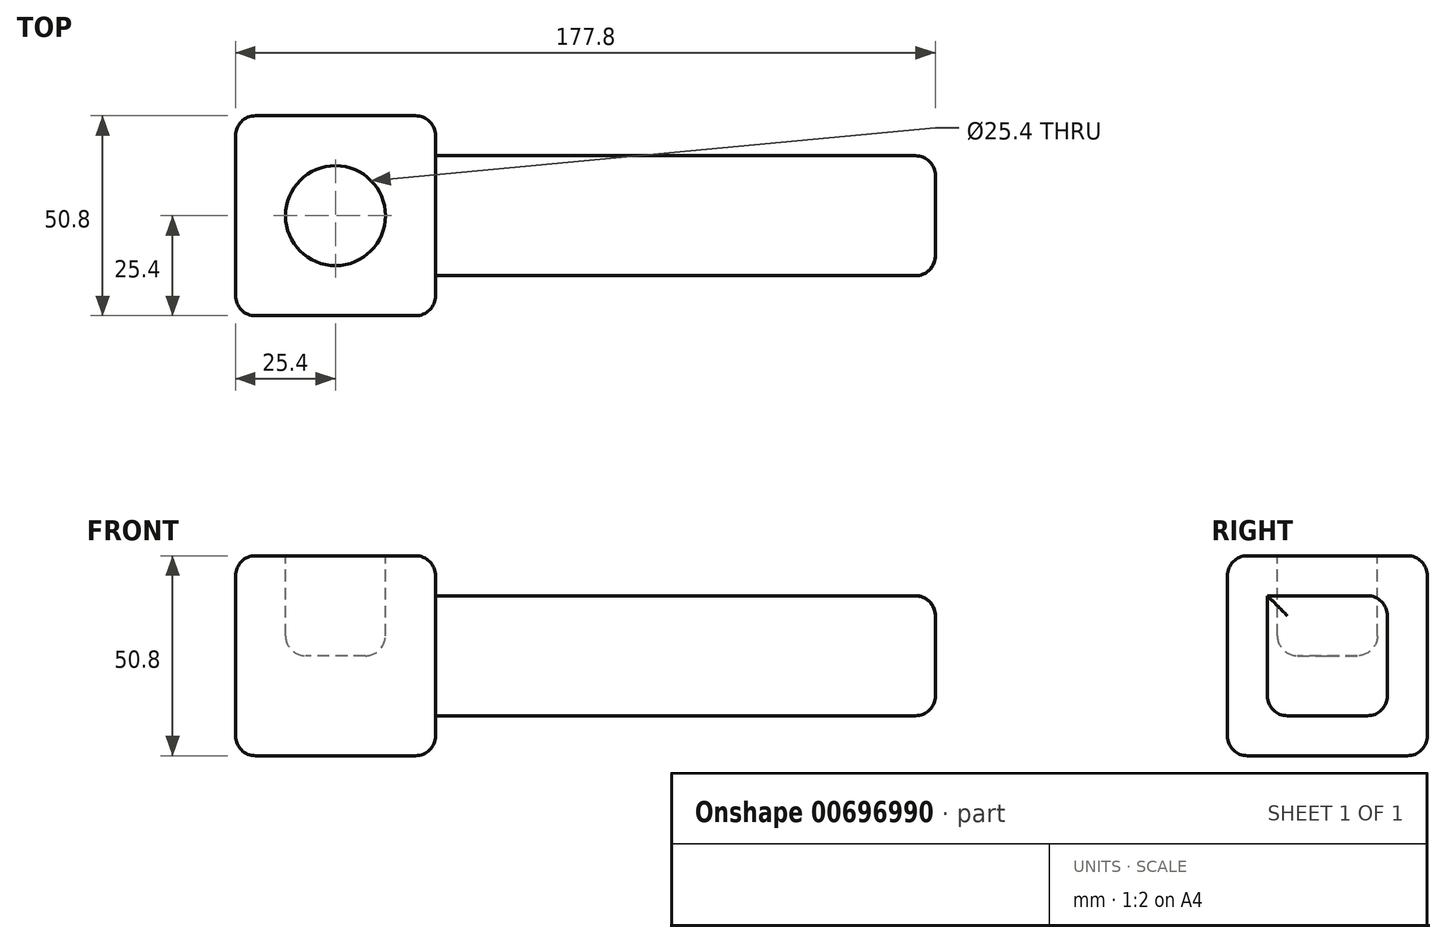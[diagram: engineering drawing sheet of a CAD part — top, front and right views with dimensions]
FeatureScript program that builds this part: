
annotation { "Feature Type Name" : "Feature", "Feature Type Description" : "" }
export const myFeature = defineFeature(function(context is Context, id is Id, definition is map)
    precondition{}
    {
        {
            var Q0;
            Q0=qCreatedBy(makeId("Top.planeOp"),FACE);
            var sketch = newSketch(context, id + "F0", { "sketchPlane" : qUnion([Q0])});
            skLineSegment(sketch, "E0.bottom", {"start": v(0, 0) * mm, "end": v(50.8, 0) * mm});
            skLineSegment(sketch, "E0.top", {"start": v(0, 50.8) * mm, "end": v(50.8, 50.8) * mm});
            skLineSegment(sketch, "E0.left", {"start": v(0, 0) * mm, "end": v(0, 50.8) * mm});
            skLineSegment(sketch, "E0.right", {"start": v(50.8, 0) * mm, "end": v(50.8, 50.8) * mm});
            skSolve(sketch);
        }
        {
            var Q0;
            Q0 = qSketchRegion(id + "F0", true);
            extrude(context, id + "F1", {"entities" : qUnion([Q0]), "depth" : 50.8 * mm, "offsetDistance" : 25.4 * mm});
        }
        {
            var Q0;
            Q0=makeQuery(id+"F1.opExtrude","CAP_FACE",FACE,{"disambiguationData":[OSD([sQuery(id+"F0.wireOp",EDGE,"E0.bottom"),sQuery(id+"F0.wireOp",EDGE,"E0.top"),sQuery(id+"F0.wireOp",EDGE,"E0.left"),sQuery(id+"F0.wireOp",EDGE,"E0.right")])],"isStart":false});
            var sketch = newSketch(context, id + "F2", { "sketchPlane" : qUnion([Q0])});
            skLineSegment(sketch, "E1", {"start": v(0, 0) * mm, "end": v(50.8, 50.8) * mm, "construction": true});
            skLineSegment(sketch, "E2", {"start": v(50.8, 0) * mm, "end": v(0, 50.8) * mm, "construction": true});
            skLineSegment(sketch, "E3", {"start": v(0, 50.8) * mm, "end": v(0.46, 49.47) * mm});
            skCircle(sketch, "E4", {"center": v(25.4, 25.4) * mm, "radius": 12.7 * mm});
            skSolve(sketch);
        }
        {
            var Q0;
            Q0 = qSketchRegion(id + "F2", true);
            extrude(context, id + "F3", {"entities" : qUnion([Q0]), "operationType" : NewBodyOperationType.REMOVE, "oppositeDirection" : true, "depth" : 25.4 * mm, "offsetDistance" : 25.4 * mm});
        }
        {
            var Q0;
            Q0=makeQuery(id+"F1.opExtrude","CAP_EDGE",EDGE,{"disambiguationData":[OSD([sQuery(id+"F0.wireOp",EDGE,"E0.top")])],"isStart":false});
            var Q1;
            Q1=makeQuery(id+"F1.opExtrude","CAP_EDGE",EDGE,{"disambiguationData":[OSD([sQuery(id+"F0.wireOp",EDGE,"E0.right")])],"isStart":false});
            var Q2;
            Q2=makeQuery(id+"F1.opExtrude","CAP_EDGE",EDGE,{"disambiguationData":[OSD([sQuery(id+"F0.wireOp",EDGE,"E0.bottom")])],"isStart":false});
            var Q3;
            Q3=makeQuery(id+"F1.opExtrude","CAP_EDGE",EDGE,{"disambiguationData":[OSD([sQuery(id+"F0.wireOp",EDGE,"E0.left")])],"isStart":false});
            var Q4;
            Q4=makeQuery(id+"F1.opExtrude","SWEPT_FACE",FACE,{"disambiguationData":[OSD([sQuery(id+"F0.wireOp",EDGE,"E0.right")])]});
            var Q5;
            Q5=makeQuery(id+"F1.opExtrude","SWEPT_FACE",FACE,{"disambiguationData":[OSD([sQuery(id+"F0.wireOp",EDGE,"E0.bottom")])]});
            var Q6;
            Q6=makeQuery(id+"F1.opExtrude","SWEPT_FACE",FACE,{"disambiguationData":[OSD([sQuery(id+"F0.wireOp",EDGE,"E0.left")])]});
            var Q7;
            Q7=makeQuery(id+"F1.opExtrude","CAP_FACE",FACE,{"disambiguationData":[OSD([sQuery(id+"F0.wireOp",EDGE,"E0.bottom"),sQuery(id+"F0.wireOp",EDGE,"E0.top"),sQuery(id+"F0.wireOp",EDGE,"E0.left"),sQuery(id+"F0.wireOp",EDGE,"E0.right")])],"isStart":true});
            fillet(context, id + "F4", {"entities" : qUnion([Q0, Q1, Q2, Q3, Q4, Q5, Q6, Q7]), "radius" : 5.08 * mm, "tangentPropagation" : true, "allowEdgeOverflow" : false});
        }
        {
            var Q0;
            Q0=makeQuery(id+"F3.boolean.opBoolean","COPY",EDGE,{"derivedFrom":makeQuery(id+"F3.opExtrude","CAP_EDGE",EDGE,{"disambiguationData":[OSD([sQuery(id+"F2.wireOp",EDGE,"E4")])],"isStart":false})});
            var Q1;
            Q1=makeQuery(id+"F3.boolean.opBoolean","COPY",EDGE,{"derivedFrom":makeQuery(id+"F3.opExtrude","CAP_EDGE",EDGE,{"disambiguationData":[OSD([sQuery(id+"F2.wireOp",EDGE,"E4")])],"isStart":true})});
            fillet(context, id + "F5", {"entities" : qUnion([Q0, Q1]), "radius" : 5.08 * mm, "tangentPropagation" : true, "allowEdgeOverflow" : false});
        }
        {
            var Q0;
            Q0=makeQuery(id+"F1.opExtrude","SWEPT_FACE",FACE,{"disambiguationData":[OSD([sQuery(id+"F0.wireOp",EDGE,"E0.right")])]});
            var sketch = newSketch(context, id + "F6", { "sketchPlane" : qUnion([Q0])});
            skLineSegment(sketch, "E5.bottom", {"start": v(10.16, 10.16) * mm, "end": v(40.64, 10.16) * mm});
            skLineSegment(sketch, "E5.top", {"start": v(10.16, 40.64) * mm, "end": v(40.64, 40.64) * mm});
            skLineSegment(sketch, "E5.left", {"start": v(10.16, 10.16) * mm, "end": v(10.16, 40.64) * mm});
            skLineSegment(sketch, "E5.right", {"start": v(40.64, 10.16) * mm, "end": v(40.64, 40.64) * mm});
            skSolve(sketch);
        }
        {
            var Q0;
            Q0 = qSketchRegion(id + "F6", true);
            extrude(context, id + "F7", {"entities" : qUnion([Q0]), "operationType" : NewBodyOperationType.ADD, "depth" : 127 * mm, "offsetDistance" : 25.4 * mm});
        }
        {
            var Q0;
            Q0=makeQuery(id+"F7.opExtrude","SWEPT_EDGE",EDGE,{"disambiguationData":[OSD([sQuery(id+"F6.wireOp",EDGE,"E5.bottom"),sQuery(id+"F6.wireOp",EDGE,"E5.left")])]});
            var Q1;
            Q1=makeQuery(id+"F7.opExtrude","SWEPT_EDGE",EDGE,{"disambiguationData":[OSD([sQuery(id+"F6.wireOp",EDGE,"E5.top"),sQuery(id+"F6.wireOp",EDGE,"E5.right")])]});
            var Q2;
            Q2=makeQuery(id+"F7.opExtrude","SWEPT_EDGE",EDGE,{"disambiguationData":[OSD([sQuery(id+"F6.wireOp",EDGE,"E5.bottom"),sQuery(id+"F6.wireOp",EDGE,"E5.right")])]});
            var Q3;
            Q3=makeQuery(id+"F7.opExtrude","CAP_EDGE",EDGE,{"disambiguationData":[OSD([sQuery(id+"F6.wireOp",EDGE,"E5.bottom")])],"isStart":false});
            var Q4;
            Q4=makeQuery(id+"F7.opExtrude","CAP_EDGE",EDGE,{"disambiguationData":[OSD([sQuery(id+"F6.wireOp",EDGE,"E5.right")])],"isStart":false});
            var Q5;
            Q5=makeQuery(id+"F7.opExtrude","CAP_EDGE",EDGE,{"disambiguationData":[OSD([sQuery(id+"F6.wireOp",EDGE,"E5.top")])],"isStart":false});
            var Q6;
            Q6=makeQuery(id+"F7.opExtrude","CAP_EDGE",EDGE,{"disambiguationData":[OSD([sQuery(id+"F6.wireOp",EDGE,"E5.left")])],"isStart":false});
            fillet(context, id + "F8", {"entities" : qUnion([Q0, Q1, Q2, Q3, Q4, Q5, Q6]), "radius" : 5.08 * mm, "tangentPropagation" : true, "allowEdgeOverflow" : false});
        }
    });
